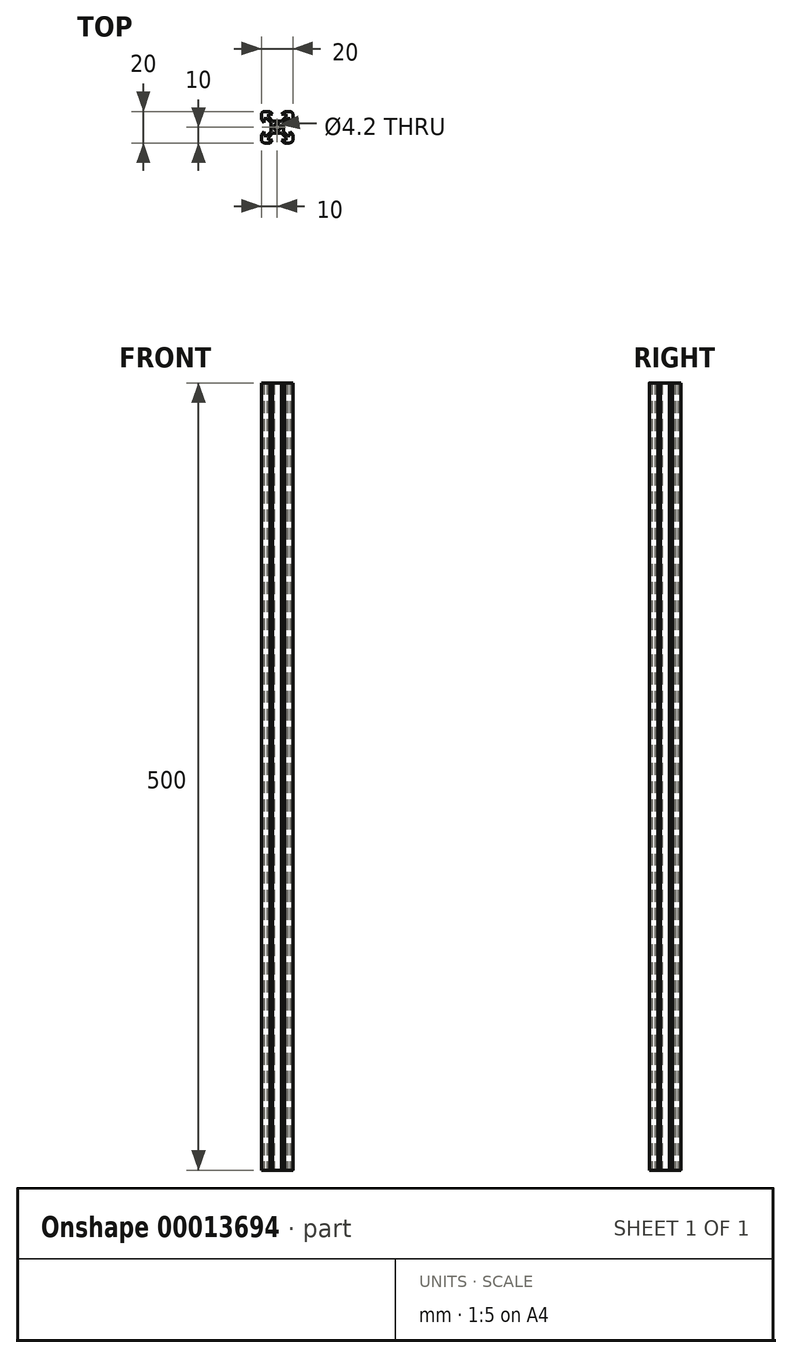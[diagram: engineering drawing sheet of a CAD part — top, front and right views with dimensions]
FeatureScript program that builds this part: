
annotation { "Feature Type Name" : "Feature", "Feature Type Description" : "" }
export const myFeature = defineFeature(function(context is Context, id is Id, definition is map)
    precondition{}
    {
        {
            var Q0;
            Q0=qCreatedBy(makeId("Top.planeOp"),FACE);
            var sketch = newSketch(context, id + "F0", { "sketchPlane" : qUnion([Q0])});
            skCircle(sketch, "E0", {"center": v(0, 0) * mm, "radius": 2.1 * mm});
            skLineSegment(sketch, "E1.rect.bottom", {"start": v(8, 10) * mm, "end": v(4.64, 10) * mm});
            skLineSegment(sketch, "E1.rect.top", {"start": v(8, -10) * mm, "end": v(4.64, -10) * mm});
            skLineSegment(sketch, "E1.rect.left", {"start": v(10, 8) * mm, "end": v(10, 4.64) * mm});
            skLineSegment(sketch, "E1.rect.right", {"start": v(-10, 8) * mm, "end": v(-10, 4.64) * mm});
            skLineSegment(sketch, "E2.0", {"start": v(5.5, 8.2) * mm, "end": v(2.84, 8.2) * mm});
            skLineSegment(sketch, "E2.1", {"start": v(8.2, 5.5) * mm, "end": v(8.2, 2.84) * mm});
            skLineSegment(sketch, "E2.2", {"start": v(5.5, -8.2) * mm, "end": v(2.84, -8.2) * mm});
            skLineSegment(sketch, "E2.3", {"start": v(-8.2, 5.5) * mm, "end": v(-8.2, 2.84) * mm});
            skLineSegment(sketch, "E3.0", {"start": v(6.56, 6.56) * mm, "end": v(-6.56, 6.56) * mm, "construction": true});
            skLineSegment(sketch, "E3.1", {"start": v(6.56, 6.56) * mm, "end": v(6.56, -6.56) * mm, "construction": true});
            skLineSegment(sketch, "E3.2", {"start": v(6.56, -6.56) * mm, "end": v(-6.56, -6.56) * mm, "construction": true});
            skLineSegment(sketch, "E3.3", {"start": v(-6.56, 6.56) * mm, "end": v(-6.56, -6.56) * mm, "construction": true});
            skLineSegment(sketch, "E4", {"start": v(0, 0) * mm, "end": v(-10, 10) * mm, "construction": true});
            skLineSegment(sketch, "E5", {"start": v(0, 0) * mm, "end": v(10, 10) * mm, "construction": true});
            skLineSegment(sketch, "E6", {"start": v(0, 0) * mm, "end": v(10, -10) * mm, "construction": true});
            skLineSegment(sketch, "E7", {"start": v(0, 0) * mm, "end": v(-10, -10) * mm, "construction": true});
            skLineSegment(sketch, "E8", {"start": v(-3.9, 2.84) * mm, "end": v(-3.9, -2.84) * mm});
            skLineSegment(sketch, "E9", {"start": v(-2.84, -3.9) * mm, "end": v(2.84, -3.9) * mm});
            skLineSegment(sketch, "E10", {"start": v(3.9, -2.84) * mm, "end": v(3.9, 2.84) * mm});
            skLineSegment(sketch, "E11", {"start": v(-2.84, 3.9) * mm, "end": v(2.84, 3.9) * mm});
            skLineSegment(sketch, "E12", {"start": v(0, 3.9) * mm, "end": v(0, 0) * mm, "construction": true});
            skLineSegment(sketch, "E13", {"start": v(3.9, 0) * mm, "end": v(0, 0) * mm, "construction": true});
            skLineSegment(sketch, "E14", {"start": v(0, -3.9) * mm, "end": v(0, 0) * mm, "construction": true});
            skLineSegment(sketch, "E15", {"start": v(-3.9, 0) * mm, "end": v(0, 0) * mm, "construction": true});
            skLineSegment(sketch, "E16", {"start": v(-2.84, 3.9) * mm, "end": v(-5.5, 6.56) * mm});
            skLineSegment(sketch, "E17", {"start": v(-3.9, 2.84) * mm, "end": v(-6.56, 5.5) * mm});
            skLineSegment(sketch, "E18", {"start": v(2.84, 3.9) * mm, "end": v(5.5, 6.56) * mm});
            skLineSegment(sketch, "E19", {"start": v(3.9, 2.84) * mm, "end": v(6.56, 5.5) * mm});
            skLineSegment(sketch, "E20", {"start": v(3.9, -2.84) * mm, "end": v(6.56, -5.5) * mm});
            skLineSegment(sketch, "E21", {"start": v(2.84, -3.9) * mm, "end": v(5.5, -6.56) * mm});
            skLineSegment(sketch, "E22", {"start": v(-2.84, -3.9) * mm, "end": v(-5.5, -6.56) * mm});
            skLineSegment(sketch, "E23", {"start": v(-3.9, -2.84) * mm, "end": v(-6.56, -5.5) * mm});
            skLineSegment(sketch, "E24", {"start": v(-5.5, -6.56) * mm, "end": v(-5.5, -8.2) * mm});
            skLineSegment(sketch, "E25", {"start": v(-6.56, -5.5) * mm, "end": v(-8.2, -5.5) * mm});
            skLineSegment(sketch, "E26", {"start": v(6.56, -5.5) * mm, "end": v(8.2, -5.5) * mm});
            skLineSegment(sketch, "E27", {"start": v(5.5, -6.56) * mm, "end": v(5.5, -8.2) * mm});
            skLineSegment(sketch, "E28", {"start": v(6.56, 5.5) * mm, "end": v(8.2, 5.5) * mm});
            skLineSegment(sketch, "E29", {"start": v(5.5, 6.56) * mm, "end": v(5.5, 8.2) * mm});
            skLineSegment(sketch, "E30", {"start": v(-5.5, 6.56) * mm, "end": v(-5.5, 8.2) * mm});
            skLineSegment(sketch, "E31", {"start": v(-6.56, 5.5) * mm, "end": v(-8.2, 5.5) * mm});
            skLineSegment(sketch, "E32", {"start": v(-8.2, -2.84) * mm, "end": v(-10, -4.64) * mm});
            skLineSegment(sketch, "E33", {"start": v(-8.2, 2.84) * mm, "end": v(-10, 4.64) * mm});
            skLineSegment(sketch, "E34", {"start": v(-2.84, 8.2) * mm, "end": v(-4.64, 10) * mm});
            skLineSegment(sketch, "E35", {"start": v(2.84, 8.2) * mm, "end": v(4.64, 10) * mm});
            skLineSegment(sketch, "E36", {"start": v(8.2, 2.84) * mm, "end": v(10, 4.64) * mm});
            skLineSegment(sketch, "E37", {"start": v(8.2, -2.84) * mm, "end": v(10, -4.64) * mm});
            skLineSegment(sketch, "E38", {"start": v(2.84, -8.2) * mm, "end": v(4.64, -10) * mm});
            skLineSegment(sketch, "E39", {"start": v(-2.84, -8.2) * mm, "end": v(-4.64, -10) * mm});
            skLineSegment(sketch, "E40.trimOffspring", {"start": v(-2.84, -8.2) * mm, "end": v(-5.5, -8.2) * mm});
            skLineSegment(sketch, "E41.trimOffspring", {"start": v(8.2, -2.84) * mm, "end": v(8.2, -5.5) * mm});
            skLineSegment(sketch, "E42.trimOffspring", {"start": v(-2.84, 8.2) * mm, "end": v(-5.5, 8.2) * mm});
            skLineSegment(sketch, "E43.trimOffspring", {"start": v(-8.2, -2.84) * mm, "end": v(-8.2, -5.5) * mm});
            skLineSegment(sketch, "E44.trimOffspring", {"start": v(-10, -4.64) * mm, "end": v(-10, -8) * mm});
            skLineSegment(sketch, "E45.trimOffspring", {"start": v(-4.64, 10) * mm, "end": v(-8, 10) * mm});
            skLineSegment(sketch, "E46.trimOffspring", {"start": v(10, -4.64) * mm, "end": v(10, -8) * mm});
            skLineSegment(sketch, "E47.trimOffspring", {"start": v(-4.64, -10) * mm, "end": v(-8, -10) * mm});
            skPoint(sketch, "E48.visualSharp", {"position": v(10, 10) * mm});
            skArc(sketch, "E48.filletArc", {"start": v(10, 8) * mm, "mid": v(9.41, 9.41) * mm, "end": v(8, 10) * mm});
            skPoint(sketch, "E49.visualSharp", {"position": v(10, -10) * mm});
            skArc(sketch, "E49.filletArc", {"start": v(8, -10) * mm, "mid": v(9.41, -9.41) * mm, "end": v(10, -8) * mm});
            skPoint(sketch, "E50.visualSharp", {"position": v(-10, -10) * mm});
            skArc(sketch, "E50.filletArc", {"start": v(-10, -8) * mm, "mid": v(-9.41, -9.41) * mm, "end": v(-8, -10) * mm});
            skPoint(sketch, "E51.visualSharp", {"position": v(-10, 10) * mm});
            skArc(sketch, "E51.filletArc", {"start": v(-8, 10) * mm, "mid": v(-9.41, 9.41) * mm, "end": v(-10, 8) * mm});
            skLineSegment(sketch, "E52", {"start": v(-14.07, 0) * mm, "end": v(-6.07, 0) * mm});
            skSolve(sketch);
        }
        {
            var Q0;
            Q0=makeQuery(id+"F0.imprint","IMPRINT",FACE,{"disambiguationData":[TD([[makeQuery(id+"F0.imprint","IMPRINT",EDGE,{"derivedFrom":sQuery(id+"F0.wireOp",EDGE,"E0")}),-1.0]])]});
            extrude(context, id + "F1", {"entities" : qUnion([Q0]), "depth" : 500 * mm});
        }
    });
